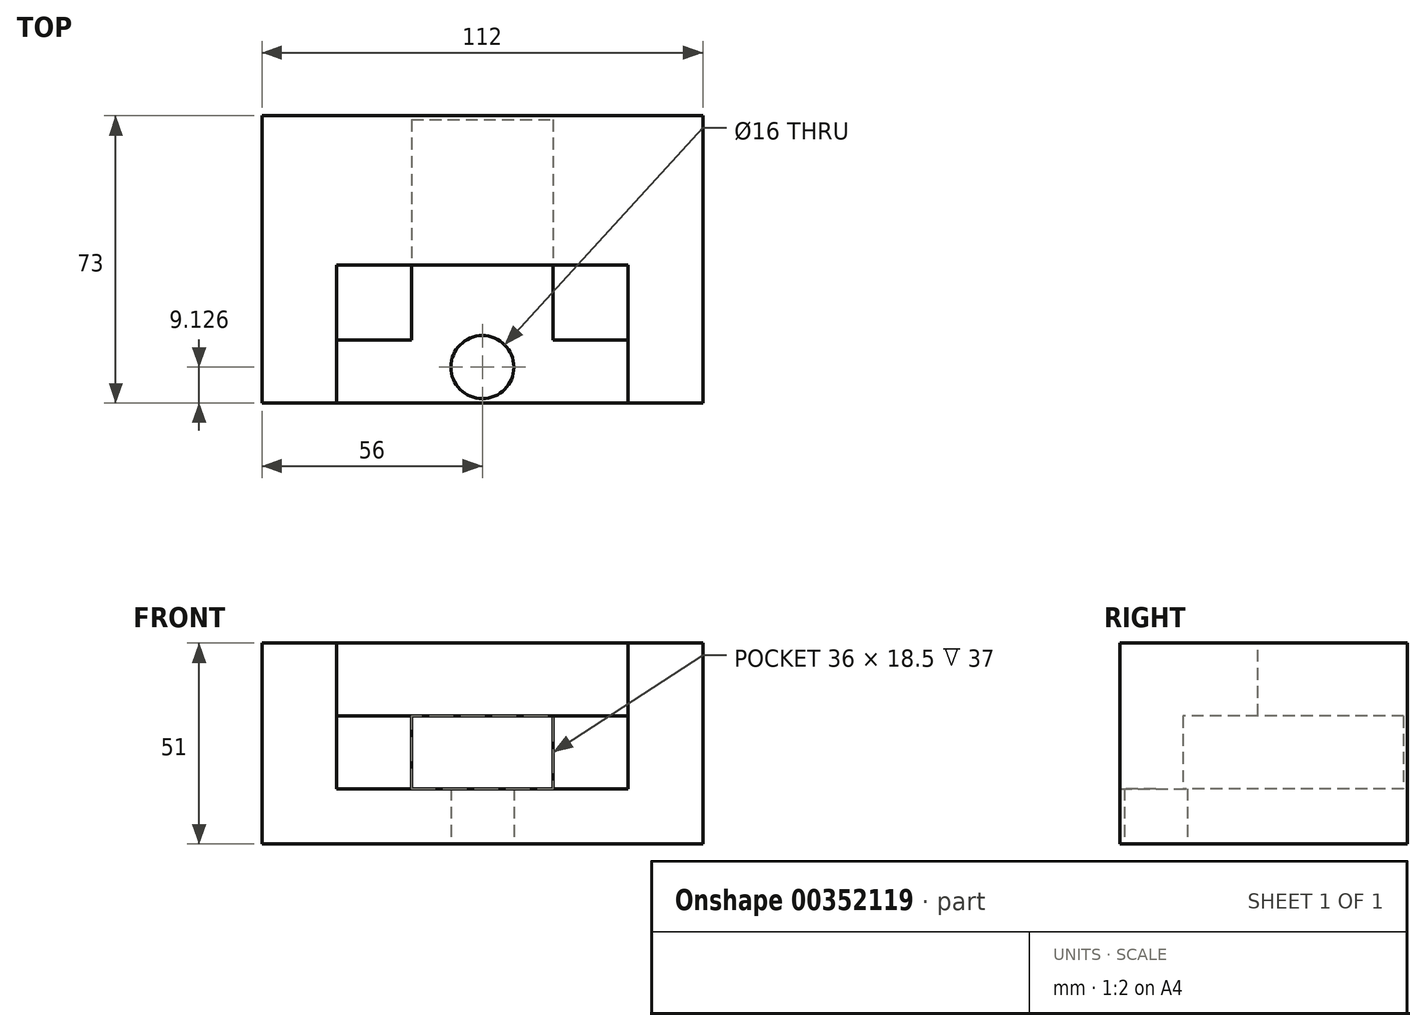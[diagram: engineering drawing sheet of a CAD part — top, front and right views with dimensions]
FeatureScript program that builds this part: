
annotation { "Feature Type Name" : "Feature", "Feature Type Description" : "" }
export const myFeature = defineFeature(function(context is Context, id is Id, definition is map)
    precondition{}
    {
        {
            var Q0;
            Q0=qCreatedBy(makeId("Front.planeOp"),FACE);
            var sketch = newSketch(context, id + "F0", { "sketchPlane" : qUnion([Q0])});
            skLineSegment(sketch, "E0.bottom", {"start": v(0, 0) * mm, "end": v(112, 0) * mm});
            skLineSegment(sketch, "E0.top", {"start": v(0, 51) * mm, "end": v(112, 51) * mm});
            skLineSegment(sketch, "E0.left", {"start": v(0, 0) * mm, "end": v(0, 51) * mm});
            skLineSegment(sketch, "E0.right", {"start": v(112, 0) * mm, "end": v(112, 51) * mm});
            skSolve(sketch);
        }
        {
            var Q0;
            Q0 = qSketchRegion(id + "F0", true);
            extrude(context, id + "F1", {"entities" : qUnion([Q0]), "depth" : 57 * mm});
        }
        {
            var Q0;
            Q0=makeQuery(id+"F1.opExtrude","CAP_FACE",FACE,{"disambiguationData":[OSD([sQuery(id+"F0.wireOp",EDGE,"E0.bottom"),sQuery(id+"F0.wireOp",EDGE,"E0.top"),sQuery(id+"F0.wireOp",EDGE,"E0.left"),sQuery(id+"F0.wireOp",EDGE,"E0.right")])],"isStart":false});
            var sketch = newSketch(context, id + "F2", { "sketchPlane" : qUnion([Q0])});
            skLineSegment(sketch, "E1", {"start": v(19, 51) * mm, "end": v(19, 14) * mm});
            skLineSegment(sketch, "E2", {"start": v(19, 14) * mm, "end": v(93, 14) * mm});
            skLineSegment(sketch, "E3", {"start": v(93, 14) * mm, "end": v(93, 51) * mm});
            skLineSegment(sketch, "E4", {"start": v(93, 51) * mm, "end": v(19, 51) * mm});
            skLineSegment(sketch, "E5", {"start": v(19, 32.5) * mm, "end": v(93, 32.5) * mm});
            skLineSegment(sketch, "E6", {"start": v(38, 32.5) * mm, "end": v(38, 14) * mm});
            skLineSegment(sketch, "E7", {"start": v(74, 32.5) * mm, "end": v(74, 14) * mm});
            skSolve(sketch);
        }
        {
            var Q0;
            {var subQ4=sQuery(id+"F2.wireOp",EDGE,"E4");Q0=makeQuery(id+"F2.imprint","IMPRINT",FACE,{"disambiguationData":[TD([[makeQuery(id+"F2.imprint","IMPRINT",EDGE,{"derivedFrom":subQ4}),-1.0]])]});}
            extrude(context, id + "F3", {"entities" : qUnion([Q0]), "operationType" : NewBodyOperationType.REMOVE, "oppositeDirection" : true, "depth" : 19 * mm});
        }
        {
            var Q0;
            Q0=makeQuery(id+"F2.imprint","IMPRINT",FACE,{"disambiguationData":[TD([[makeQuery(id+"F2.imprint","IMPRINT",EDGE,{"derivedFrom":makeQuery(id+"F1.opExtrude","CAP_EDGE",EDGE,{"disambiguationData":[OSD([sQuery(id+"F0.wireOp",EDGE,"E0.bottom")])],"isStart":false})}),1.0]])]});
            extrude(context, id + "F4", {"entities" : qUnion([Q0]), "operationType" : NewBodyOperationType.ADD, "depth" : 16 * mm});
        }
        {
            var Q0;
            {var subQ0=sQuery(id+"F2.wireOp",EDGE,"E6");Q0=makeQuery(id+"F2.imprint","IMPRINT",FACE,{"disambiguationData":[TD([[makeQuery(id+"F2.imprint","IMPRINT",EDGE,{"derivedFrom":subQ0}),1.0]])]});}
            extrude(context, id + "F5", {"entities" : qUnion([Q0]), "operationType" : NewBodyOperationType.REMOVE, "oppositeDirection" : true, "depth" : 56 * mm});
        }
        {
            var Q0;
            {var subQ0=sQuery(id+"F0.wireOp",EDGE,"E0.bottom");Q0=makeQuery(id+"F4.boolean.opBoolean","MERGE",FACE,{"derivedFrom":[makeQuery(id+"F1.opExtrude","SWEPT_FACE",FACE,{"disambiguationData":[OSD([subQ0])]}),makeQuery(id+"F4.opExtrude","SWEPT_FACE",FACE,{"disambiguationData":[OSD([subQ0])]})]});}
            var sketch = newSketch(context, id + "F6", { "sketchPlane" : qUnion([Q0])});
            skCircle(sketch, "E8", {"center": v(56, 63.87) * mm, "radius": 8 * mm});
            skSolve(sketch);
        }
        {
            var Q0;
            Q0 = qSketchRegion(id + "F6", true);
            extrude(context, id + "F7", {"entities" : qUnion([Q0]), "operationType" : NewBodyOperationType.REMOVE, "oppositeDirection" : true, "depth" : 16 * mm});
        }
    });
